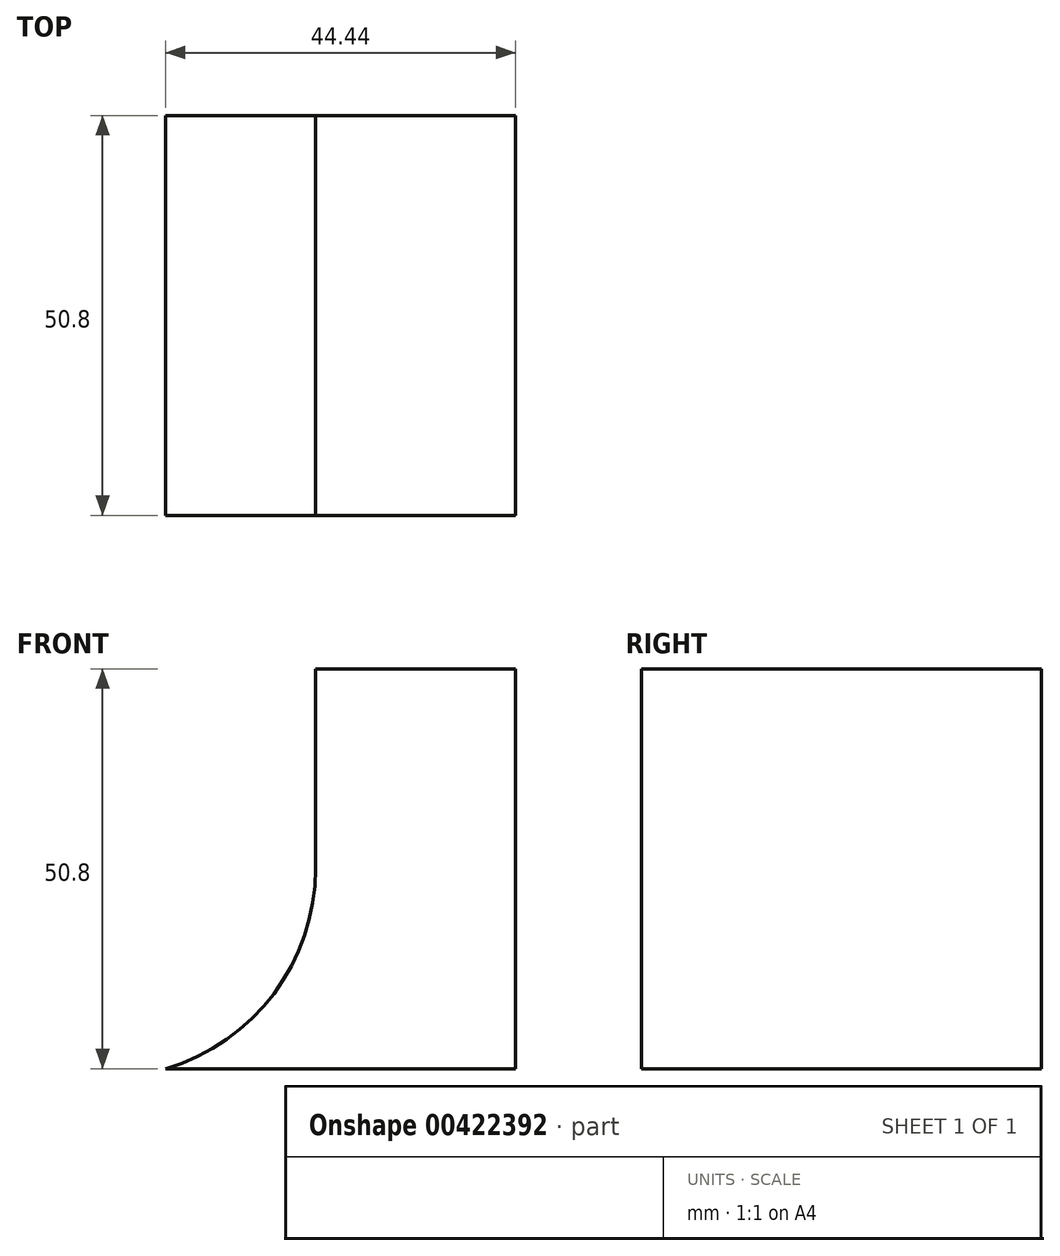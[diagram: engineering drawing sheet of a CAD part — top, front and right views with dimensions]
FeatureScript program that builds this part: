
annotation { "Feature Type Name" : "Feature", "Feature Type Description" : "" }
export const myFeature = defineFeature(function(context is Context, id is Id, definition is map)
    precondition{}
    {
        {
            var Q0;
            Q0=qCreatedBy(makeId("Front.planeOp"),FACE);
            var sketch = newSketch(context, id + "F0", { "sketchPlane" : qUnion([Q0])});
            skLineSegment(sketch, "E0", {"start": v(0, 0) * mm, "end": v(0, 50.8) * mm});
            skLineSegment(sketch, "E1", {"start": v(-25.4, 50.8) * mm, "end": v(0, 50.8) * mm});
            skLineSegment(sketch, "E2", {"start": v(-25.4, 50.8) * mm, "end": v(-25.4, 25.4) * mm});
            skLineSegment(sketch, "E3", {"start": v(-44.44, 0) * mm, "end": v(0, 0) * mm});
            skArc(sketch, "E4", {"start": v(-44.44, 0) * mm, "mid": v(-30.69, 9.53) * mm, "end": v(-25.4, 25.4) * mm});
            skSolve(sketch);
        }
        {
            var Q0;
            Q0 = qSketchRegion(id + "F0", true);
            extrude(context, id + "F1", {"entities" : qUnion([Q0]), "depth" : 50.8 * mm});
        }
    });
